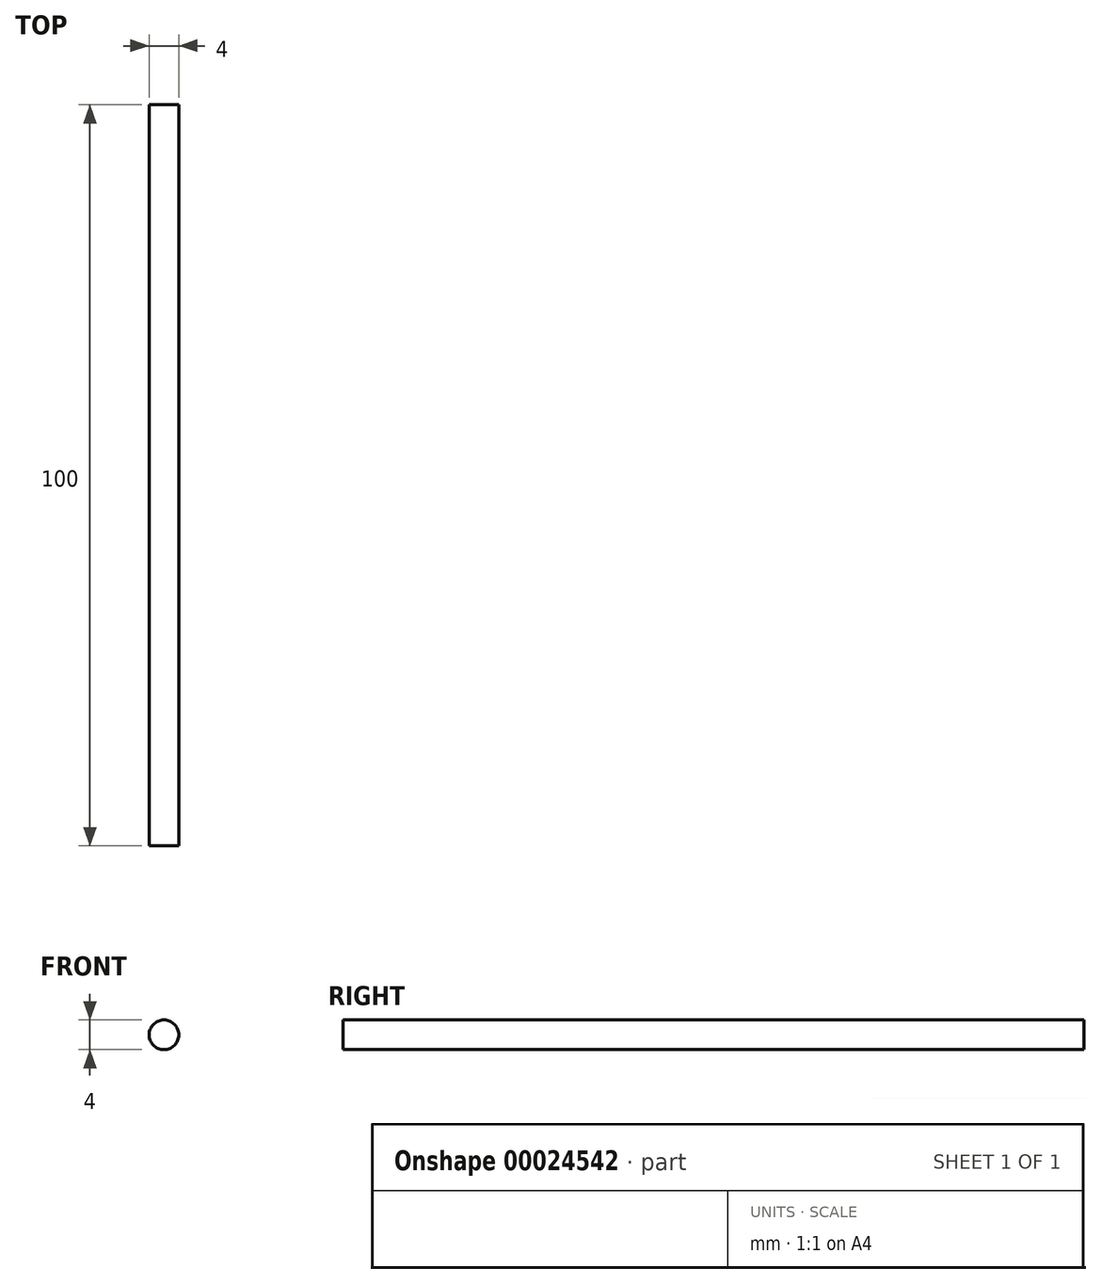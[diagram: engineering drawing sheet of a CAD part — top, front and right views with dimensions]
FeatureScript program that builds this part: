
annotation { "Feature Type Name" : "Feature", "Feature Type Description" : "" }
export const myFeature = defineFeature(function(context is Context, id is Id, definition is map)
    precondition{}
    {
        {
            var Q0;
            Q0=qCreatedBy(makeId("Front.planeOp"),FACE);
            var sketch = newSketch(context, id + "F0", { "sketchPlane" : qUnion([Q0])});
            skCircle(sketch, "E0", {"center": v(0, 0) * mm, "radius": 2 * mm});
            skSolve(sketch);
        }
        {
            var Q0;
            Q0=makeQuery(id+"F0.imprint","IMPRINT",FACE,{"disambiguationData":[TD([[makeQuery(id+"F0.imprint","IMPRINT",EDGE,{"derivedFrom":sQuery(id+"F0.wireOp",EDGE,"E0")}),1.0]])]});
            extrude(context, id + "F1", {"entities" : qUnion([Q0]), "depth" : 100 * mm});
        }
    });
